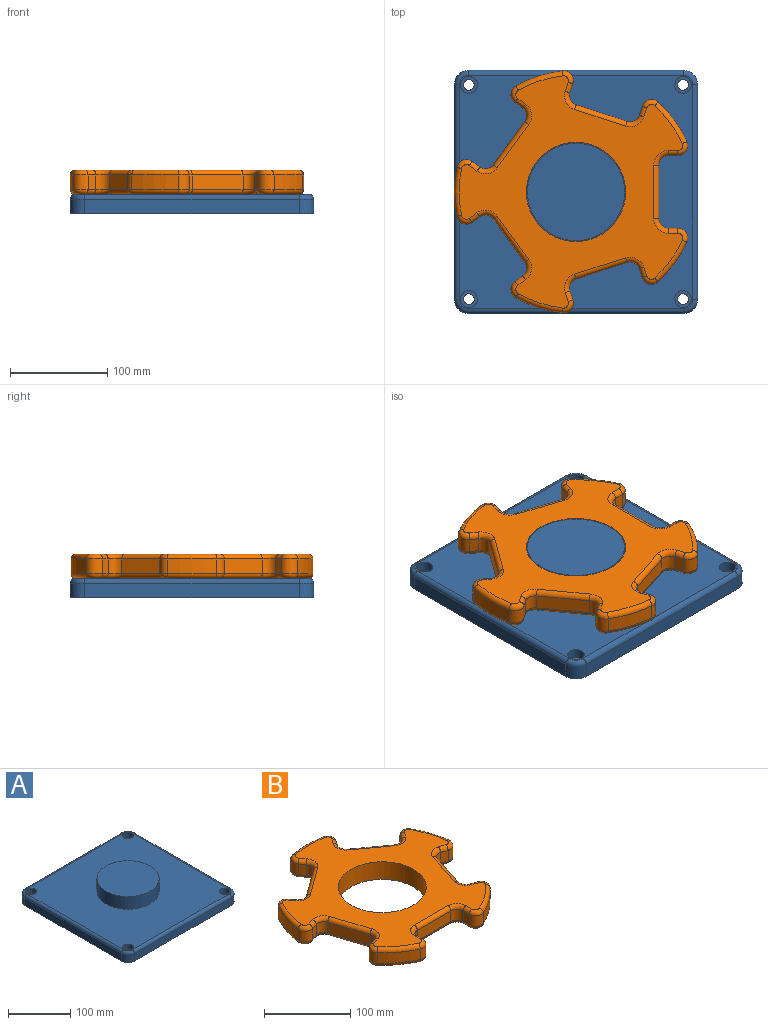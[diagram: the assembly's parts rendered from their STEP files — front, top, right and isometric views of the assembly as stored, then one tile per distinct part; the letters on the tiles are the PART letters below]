
ASSEMBLY  parts=2 mates=1
PART A: 32 faces, bbox 252.5x252.5x45 mm
  f0: plane 220x15mm, normal (1,0,0), area 3300mm2, adj f5,f8,f11,f27
  f1: plane 220x15mm, normal (0,1,0), area 3300mm2, adj f5,f8,f9,f31
  f2: plane 220x15mm, normal (-1,0,0), area 3300mm2, adj f5,f9,f10,f28
  f3: plane 220x15mm, normal (0,-1,0), area 3300mm2, adj f5,f10,f11,f24
  f4: plane 240x240mm, normal (0,0,1), area 48725.4mm2, adj f6,f14,f17,f20,f23,f24,f25,f26
  f5: plane 250x250mm, normal (0,0,-1), area 61926.7mm2, adj f0,f1,f2,f3,f8,f9,f10,f11
  f6: cylinder r=50mm len=100mm, axis (0,0,-1), area 7854mm2, adj f4,f7
  f7: plane 100x100mm, normal (0,0,1), area 7854mm2, adj f6
  f8: cylinder r=15mm len=15mm, axis (0,0,-1), area 353.4mm2, adj f0,f1,f5,f29
  f9: cylinder r=15mm len=15mm, axis (0,0,1), area 353.4mm2, adj f1,f2,f5,f30
  f10: cylinder r=15mm len=15mm, axis (0,0,-1), area 353.4mm2, adj f2,f3,f5,f26
  f11: cylinder r=15mm len=15mm, axis (0,0,1), area 353.4mm2, adj f0,f3,f5,f25
  f12: cylinder r=5.5mm len=11mm, axis (0,0,1), area 345.6mm2, adj f5,f13
  f13: plane 17.25x17.25mm, normal (0,0,1), area 138.7mm2, adj f12,f14
  f14: cylinder r=8.62mm len=17.25mm, axis (0,0,1), area 541.9mm2, adj f4,f13
  f15: cylinder r=5.5mm len=11mm, axis (0,0,1), area 345.6mm2, adj f5,f16
  f16: plane 17.25x17.25mm, normal (0,0,1), area 138.7mm2, adj f15,f17
  f17: cylinder r=8.62mm len=17.25mm, axis (0,0,1), area 541.9mm2, adj f4,f16
  f18: cylinder r=5.5mm len=11mm, axis (0,0,1), area 345.6mm2, adj f5,f19
  f19: plane 17.25x17.25mm, normal (0,0,1), area 138.7mm2, adj f18,f20
  f20: cylinder r=8.62mm len=17.25mm, axis (0,0,1), area 541.9mm2, adj f4,f19
  f21: cylinder r=5.5mm len=11mm, axis (0,0,1), area 345.6mm2, adj f5,f22
  f22: plane 17.25x17.25mm, normal (0,0,1), area 138.7mm2, adj f21,f23
  f23: cylinder r=8.62mm len=17.25mm, axis (0,0,1), area 541.9mm2, adj f4,f22
  f24: cylinder r=5mm len=220mm, axis (-1,0,0), area 1727.9mm2, adj f3,f4,f25,f26
  f25: torus R=10mm, axis (0,0,1), area 162.6mm2, adj f4,f11,f24,f27
  f26: torus R=10mm, axis (0,0,1), area 162.6mm2, adj f4,f10,f24,f28
  f27: cylinder r=5mm len=220mm, axis (0,-1,0), area 1727.9mm2, adj f0,f4,f25,f29
  f28: cylinder r=5mm len=220mm, axis (0,1,0), area 1727.9mm2, adj f2,f4,f26,f30
  f29: torus R=10mm, axis (0,0,1), area 162.6mm2, adj f4,f8,f27,f31
  f30: torus R=10mm, axis (0,0,1), area 162.6mm2, adj f4,f9,f28,f31
  f31: cylinder r=5mm len=220mm, axis (1,0,0), area 1727.9mm2, adj f1,f4,f29,f30
PART B: 123 faces, bbox 268.9x258.5x25 mm
  f0: plane 238.57x229.73mm, normal (0,0,1), area 21505.7mm2, adj f6,f83,f84,f85,f86,f87,f88,f89
  f1: plane 238.57x229.73mm, normal (0,0,-1), area 21505.7mm2, adj f6,f43,f44,f45,f46,f47,f48,f49
  f2: cylinder r=125mm len=47.82mm, axis (0,0,-1), area 759.5mm2, adj f34,f42,f74,f114
  f3: cylinder r=125mm len=50.29mm, axis (0,0,-1), area 759.5mm2, adj f27,f35,f75,f115
  f4: cylinder r=125mm len=47.82mm, axis (0,0,-1), area 759.5mm2, adj f20,f28,f59,f99
  f5: cylinder r=125mm len=40.68mm, axis (0,0,-1), area 759.5mm2, adj f13,f21,f43,f83
  f6: cylinder r=51mm len=102mm, axis (0,0,-1), area 8011.1mm2, adj f0,f1
  f7: cylinder r=125mm len=40.68mm, axis (0,0,-1), area 759.5mm2, adj f14,f41,f58,f98
  f8: plane 15x9.73mm, normal (-1,0,0), area 146mm2, adj f11,f14,f54,f94
  f9: plane 55x15mm, normal (0,-1,0), area 825mm2, adj f11,f12,f50,f90
  f10: plane 15x9.73mm, normal (1,0,0), area 146mm2, adj f12,f13,f46,f86
  f11: cylinder r=10mm len=15mm, axis (0,0,-1), area 235.6mm2, adj f8,f9,f52,f92
  f12: cylinder r=10mm len=15mm, axis (0,0,-1), area 235.6mm2, adj f9,f10,f48,f88
  f13: cylinder r=10mm len=15mm, axis (0,0,-1), area 299.5mm2, adj f5,f10,f44,f84
  f14: cylinder r=10mm len=15mm, axis (0,0,-1), area 299.5mm2, adj f7,f8,f56,f96
  f15: plane 15x9.26mm, normal (-0.31,0.95,0), area 146mm2, adj f18,f21,f47,f87
  f16: plane 52.31x17mm, normal (-0.95,-0.31,0), area 825mm2, adj f18,f19,f51,f91
  f17: plane 15x9.26mm, normal (0.31,-0.95,0), area 146mm2, adj f19,f20,f55,f95
  f18: cylinder r=10mm len=15mm, axis (0,0,-1), area 235.6mm2, adj f15,f16,f49,f89
  f19: cylinder r=10mm len=15mm, axis (0,0,-1), area 235.6mm2, adj f16,f17,f53,f93
  f20: cylinder r=10mm len=15mm, axis (0,0,-1), area 299.5mm2, adj f4,f17,f57,f97
  f21: cylinder r=10mm len=16.25mm, axis (0,0,-1), area 299.5mm2, adj f5,f15,f45,f85
  f22: plane 15x7.87mm, normal (0.81,0.59,0), area 146mm2, adj f25,f28,f63,f103
  f23: plane 44.5x32.33mm, normal (-0.59,0.81,0), area 825mm2, adj f25,f26,f67,f107
  f24: plane 15x7.87mm, normal (-0.81,-0.59,0), area 146mm2, adj f26,f27,f71,f111
  f25: cylinder r=10mm len=15mm, axis (0,0,-1), area 235.6mm2, adj f22,f23,f65,f105
  f26: cylinder r=10mm len=15mm, axis (0,0,-1), area 235.6mm2, adj f23,f24,f69,f109
  f27: cylinder r=10mm len=15.67mm, axis (0,0,-1), area 299.5mm2, adj f3,f24,f73,f113
  f28: cylinder r=10mm len=16.78mm, axis (0,0,-1), area 299.5mm2, adj f4,f22,f61,f101
  f29: plane 15x7.87mm, normal (0.81,-0.59,0), area 146mm2, adj f32,f35,f79,f119
  f30: plane 44.5x32.33mm, normal (0.59,0.81,0), area 825mm2, adj f32,f33,f82,f122
  f31: plane 15x7.87mm, normal (-0.81,0.59,0), area 146mm2, adj f33,f34,f78,f118
  f32: cylinder r=10mm len=15mm, axis (0,0,-1), area 235.6mm2, adj f29,f30,f81,f121
  f33: cylinder r=10mm len=15mm, axis (0,0,-1), area 235.6mm2, adj f30,f31,f80,f120
  f34: cylinder r=10mm len=16.78mm, axis (0,0,-1), area 299.5mm2, adj f2,f31,f76,f116
  f35: cylinder r=10mm len=15.67mm, axis (0,0,-1), area 299.5mm2, adj f3,f29,f77,f117
  f36: plane 15x9.26mm, normal (-0.31,-0.95,0), area 146mm2, adj f39,f42,f70,f110
  f37: plane 52.31x17mm, normal (0.95,-0.31,0), area 825mm2, adj f39,f40,f66,f106
  f38: plane 15x9.26mm, normal (0.31,0.95,0), area 146mm2, adj f40,f41,f62,f102
  f39: cylinder r=10mm len=15mm, axis (0,0,-1), area 235.6mm2, adj f36,f37,f68,f108
  f40: cylinder r=10mm len=15mm, axis (0,0,-1), area 235.6mm2, adj f37,f38,f64,f104
  f41: cylinder r=10mm len=16.25mm, axis (0,0,-1), area 299.5mm2, adj f7,f38,f60,f100
  f42: cylinder r=10mm len=15mm, axis (0,0,-1), area 299.5mm2, adj f2,f36,f72,f112
  f43: torus R=120mm, axis (0,0,1), area 391.9mm2, adj f1,f5,f44,f45
  f44: torus R=5mm, axis (0,0,1), area 128.3mm2, adj f1,f13,f43,f46
  f45: torus R=5mm, axis (0,0,1), area 128.3mm2, adj f1,f21,f43,f47
  f46: cylinder r=5mm len=9.73mm, axis (0,-1,0), area 76.4mm2, adj f1,f10,f44,f48
  f47: cylinder r=5mm len=10.8mm, axis (0.95,0.31,0), area 76.4mm2, adj f1,f15,f45,f49
  f48: torus R=15mm, axis (0,0,1), area 145.8mm2, adj f1,f12,f46,f50
  f49: torus R=15mm, axis (0,0,1), area 145.8mm2, adj f1,f18,f47,f51
  f50: cylinder r=5mm len=55mm, axis (-1,0,0), area 432mm2, adj f1,f9,f48,f52
  f51: cylinder r=5mm len=53.85mm, axis (-0.31,0.95,0), area 432mm2, adj f1,f16,f49,f53
  f52: torus R=15mm, axis (0,0,1), area 145.8mm2, adj f1,f11,f50,f54
  f53: torus R=15mm, axis (0,0,1), area 145.8mm2, adj f1,f19,f51,f55
  f54: cylinder r=5mm len=9.73mm, axis (0,1,0), area 76.4mm2, adj f1,f8,f52,f56
  f55: cylinder r=5mm len=10.8mm, axis (-0.95,-0.31,0), area 76.4mm2, adj f1,f17,f53,f57
  f56: torus R=5mm, axis (0,0,1), area 128.3mm2, adj f1,f14,f54,f58
  f57: torus R=5mm, axis (0,0,1), area 128.3mm2, adj f1,f20,f55,f59
  f58: torus R=120mm, axis (0,0,1), area 391.9mm2, adj f1,f7,f56,f60
  f59: torus R=120mm, axis (0,0,1), area 391.9mm2, adj f1,f4,f57,f61
  f60: torus R=5mm, axis (0,0,1), area 128.3mm2, adj f1,f41,f58,f62
  f61: torus R=5mm, axis (0,0,1), area 128.3mm2, adj f1,f28,f59,f63
  f62: cylinder r=5mm len=10.8mm, axis (0.95,-0.31,0), area 76.4mm2, adj f1,f38,f60,f64
  f63: cylinder r=5mm len=10.81mm, axis (0.59,-0.81,0), area 76.4mm2, adj f1,f22,f61,f65
  f64: torus R=15mm, axis (0,0,1), area 145.8mm2, adj f1,f40,f62,f66
  f65: torus R=15mm, axis (0,0,1), area 145.8mm2, adj f1,f25,f63,f67
  f66: cylinder r=5mm len=53.85mm, axis (-0.31,-0.95,0), area 432mm2, adj f1,f37,f64,f68
  f67: cylinder r=5mm len=47.44mm, axis (0.81,0.59,0), area 432mm2, adj f1,f23,f65,f69
  f68: torus R=15mm, axis (0,0,1), area 145.8mm2, adj f1,f39,f66,f70
  f69: torus R=15mm, axis (0,0,1), area 145.8mm2, adj f1,f26,f67,f71
  f70: cylinder r=5mm len=10.8mm, axis (-0.95,0.31,0), area 76.4mm2, adj f1,f36,f68,f72
  f71: cylinder r=5mm len=10.81mm, axis (-0.59,0.81,0), area 76.4mm2, adj f1,f24,f69,f73
  f72: torus R=5mm, axis (0,0,1), area 128.3mm2, adj f1,f42,f70,f74
  f73: torus R=5mm, axis (0,0,1), area 128.3mm2, adj f1,f27,f71,f75
  f74: torus R=120mm, axis (0,0,1), area 391.9mm2, adj f1,f2,f72,f76
  f75: torus R=120mm, axis (0,0,1), area 391.9mm2, adj f1,f3,f73,f77
  f76: torus R=5mm, axis (0,0,1), area 128.3mm2, adj f1,f34,f74,f78
  f77: torus R=5mm, axis (0,0,1), area 128.3mm2, adj f1,f35,f75,f79
  f78: cylinder r=5mm len=10.81mm, axis (0.59,0.81,0), area 76.4mm2, adj f1,f31,f76,f80
  f79: cylinder r=5mm len=10.81mm, axis (-0.59,-0.81,0), area 76.4mm2, adj f1,f29,f77,f81
  f80: torus R=15mm, axis (0,0,1), area 145.8mm2, adj f1,f33,f78,f82
  f81: torus R=15mm, axis (0,0,1), area 145.8mm2, adj f1,f32,f79,f82
  f82: cylinder r=5mm len=47.44mm, axis (0.81,-0.59,0), area 432mm2, adj f1,f30,f80,f81
  f83: torus R=120mm, axis (0,0,1), area 391.9mm2, adj f0,f5,f84,f85
  f84: torus R=5mm, axis (0,0,1), area 128.3mm2, adj f0,f13,f83,f86
  f85: torus R=5mm, axis (0,0,1), area 128.3mm2, adj f0,f21,f83,f87
  f86: cylinder r=5mm len=9.73mm, axis (0,1,0), area 76.4mm2, adj f0,f10,f84,f88
  f87: cylinder r=5mm len=10.8mm, axis (-0.95,-0.31,0), area 76.4mm2, adj f0,f15,f85,f89
  f88: torus R=15mm, axis (0,0,1), area 145.8mm2, adj f0,f12,f86,f90
  f89: torus R=15mm, axis (0,0,1), area 145.8mm2, adj f0,f18,f87,f91
  f90: cylinder r=5mm len=55mm, axis (1,0,0), area 432mm2, adj f0,f9,f88,f92
  f91: cylinder r=5mm len=53.85mm, axis (0.31,-0.95,0), area 432mm2, adj f0,f16,f89,f93
  f92: torus R=15mm, axis (0,0,1), area 145.8mm2, adj f0,f11,f90,f94
  f93: torus R=15mm, axis (0,0,1), area 145.8mm2, adj f0,f19,f91,f95
  f94: cylinder r=5mm len=9.73mm, axis (0,-1,0), area 76.4mm2, adj f0,f8,f92,f96
  f95: cylinder r=5mm len=10.8mm, axis (0.95,0.31,0), area 76.4mm2, adj f0,f17,f93,f97
  f96: torus R=5mm, axis (0,0,1), area 128.3mm2, adj f0,f14,f94,f98
  f97: torus R=5mm, axis (0,0,1), area 128.3mm2, adj f0,f20,f95,f99
  f98: torus R=120mm, axis (0,0,1), area 391.9mm2, adj f0,f7,f96,f100
  f99: torus R=120mm, axis (0,0,1), area 391.9mm2, adj f0,f4,f97,f101
  f100: torus R=5mm, axis (0,0,1), area 128.3mm2, adj f0,f41,f98,f102
  f101: torus R=5mm, axis (0,0,1), area 128.3mm2, adj f0,f28,f99,f103
  f102: cylinder r=5mm len=10.8mm, axis (-0.95,0.31,0), area 76.4mm2, adj f0,f38,f100,f104
  f103: cylinder r=5mm len=10.81mm, axis (-0.59,0.81,0), area 76.4mm2, adj f0,f22,f101,f105
  f104: torus R=15mm, axis (0,0,1), area 145.8mm2, adj f0,f40,f102,f106
  f105: torus R=15mm, axis (0,0,1), area 145.8mm2, adj f0,f25,f103,f107
  f106: cylinder r=5mm len=53.85mm, axis (0.31,0.95,0), area 432mm2, adj f0,f37,f104,f108
  f107: cylinder r=5mm len=47.44mm, axis (-0.81,-0.59,0), area 432mm2, adj f0,f23,f105,f109
  f108: torus R=15mm, axis (0,0,1), area 145.8mm2, adj f0,f39,f106,f110
  f109: torus R=15mm, axis (0,0,1), area 145.8mm2, adj f0,f26,f107,f111
  f110: cylinder r=5mm len=10.8mm, axis (0.95,-0.31,0), area 76.4mm2, adj f0,f36,f108,f112
  f111: cylinder r=5mm len=10.81mm, axis (0.59,-0.81,0), area 76.4mm2, adj f0,f24,f109,f113
  f112: torus R=5mm, axis (0,0,1), area 128.3mm2, adj f0,f42,f110,f114
  f113: torus R=5mm, axis (0,0,1), area 128.3mm2, adj f0,f27,f111,f115
  f114: torus R=120mm, axis (0,0,1), area 391.9mm2, adj f0,f2,f112,f116
  f115: torus R=120mm, axis (0,0,1), area 391.9mm2, adj f0,f3,f113,f117
  f116: torus R=5mm, axis (0,0,1), area 128.3mm2, adj f0,f34,f114,f118
  f117: torus R=5mm, axis (0,0,1), area 128.3mm2, adj f0,f35,f115,f119
  f118: cylinder r=5mm len=10.81mm, axis (-0.59,-0.81,0), area 76.4mm2, adj f0,f31,f116,f120
  f119: cylinder r=5mm len=10.81mm, axis (0.59,0.81,0), area 76.4mm2, adj f0,f29,f117,f121
  f120: torus R=15mm, axis (0,0,1), area 145.8mm2, adj f0,f33,f118,f122
  f121: torus R=15mm, axis (0,0,1), area 145.8mm2, adj f0,f32,f119,f122
  f122: cylinder r=5mm len=47.44mm, axis (-0.81,0.59,0), area 432mm2, adj f0,f30,f120,f121
PLACE A at identity fixed
PLACE B rot(axis=(0,0,1),90deg) t=(0,0,0)mm
MATE revolute B.f2 <-> A.f6  axis (0,0,-1) through (0,0,20)mm
